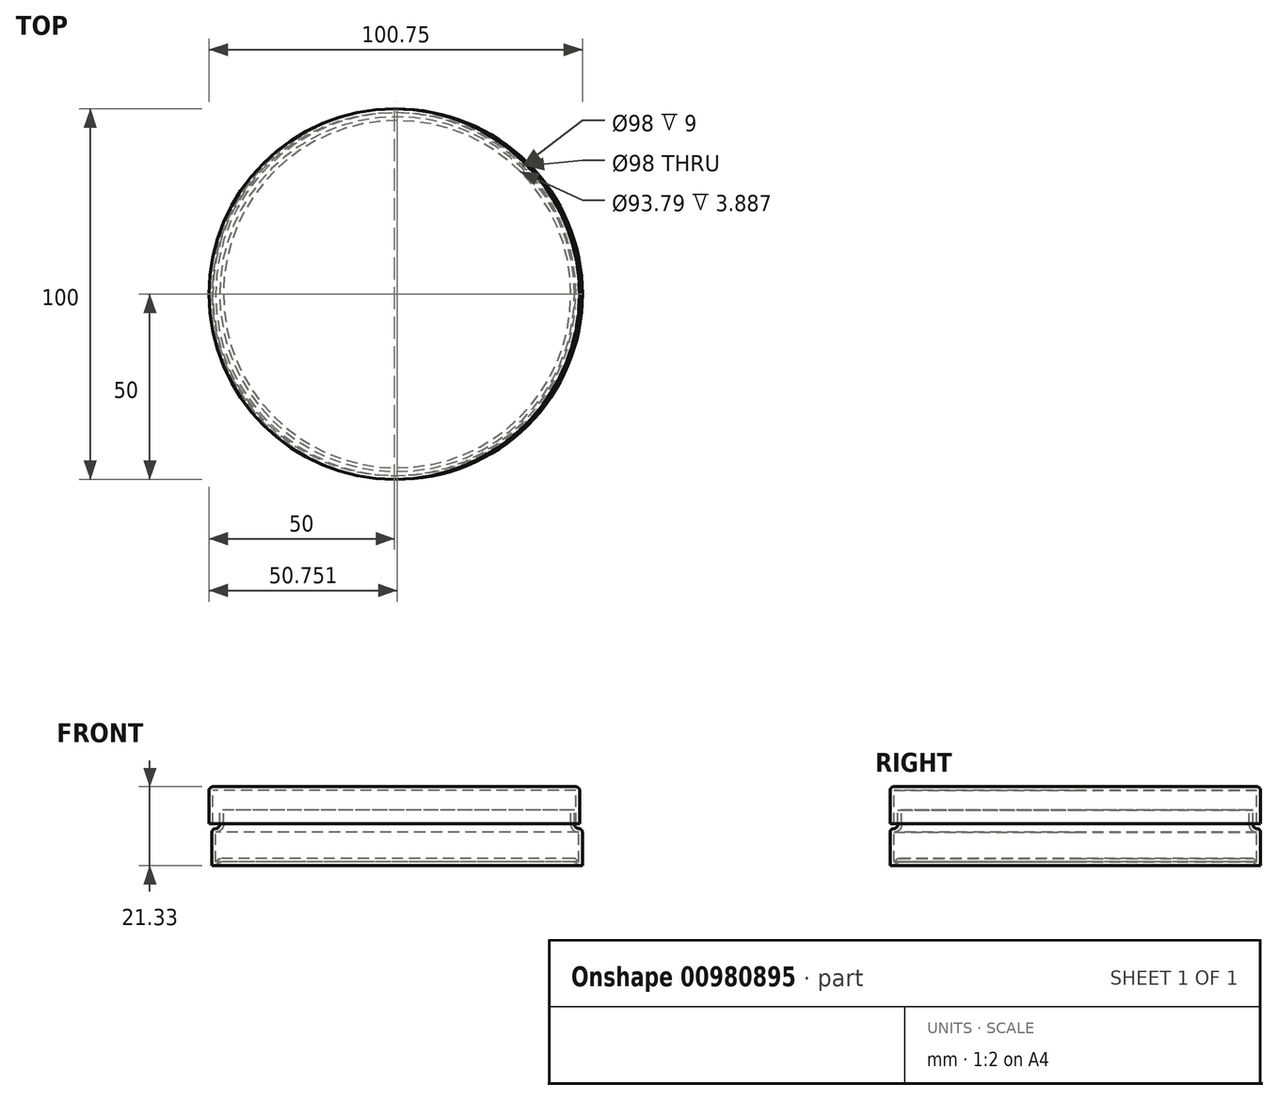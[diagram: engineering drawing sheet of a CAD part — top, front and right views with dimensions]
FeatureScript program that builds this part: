
annotation { "Feature Type Name" : "Feature", "Feature Type Description" : "" }
export const myFeature = defineFeature(function(context is Context, id is Id, definition is map)
    precondition{}
    {
        {
            var Q0;
            Q0=qCreatedBy(makeId("Front.planeOp"),FACE);
            var sketch = newSketch(context, id + "F0", { "sketchPlane" : qUnion([Q0])});
            skLineSegment(sketch, "E0", {"start": v(-50, 0) * mm, "end": v(-50, 9) * mm});
            skLineSegment(sketch, "E1", {"start": v(-49, 10) * mm, "end": v(0, 10) * mm});
            skLineSegment(sketch, "E2", {"start": v(0, 10) * mm, "end": v(0, 9) * mm});
            skLineSegment(sketch, "E3", {"start": v(0, 9) * mm, "end": v(-49, 9) * mm});
            skLineSegment(sketch, "E4", {"start": v(-49, 9) * mm, "end": v(-49, 0) * mm});
            skLineSegment(sketch, "E5", {"start": v(-49, 0) * mm, "end": v(-50, 0) * mm});
            skPoint(sketch, "E6.visualSharp", {"position": v(-50, 10) * mm});
            skArc(sketch, "E6.filletArc", {"start": v(-49, 10) * mm, "mid": v(-49.7, 9.7) * mm, "end": v(-50, 9) * mm});
            skSolve(sketch);
        }
        {
            var Q0;
            Q0=qCreatedBy(makeId("Front.planeOp"),FACE);
            var sketch = newSketch(context, id + "F1", { "sketchPlane" : qUnion([Q0])});
            skLineSegment(sketch, "E7", {"start": v(-46.15, 3.67) * mm, "end": v(-46.15, -0.22) * mm});
            skLineSegment(sketch, "E8", {"start": v(-48.25, -10.33) * mm, "end": v(-48.25, -10.33) * mm});
            skLineSegment(sketch, "E9", {"start": v(-48.25, -10.33) * mm, "end": v(-47.54, -9.62) * mm});
            skLineSegment(sketch, "E10", {"start": v(-46.83, -9.33) * mm, "end": v(0.75, -9.33) * mm});
            skLineSegment(sketch, "E11", {"start": v(0.75, -9.33) * mm, "end": v(0.75, -10.33) * mm});
            skLineSegment(sketch, "E12", {"start": v(0.75, -10.33) * mm, "end": v(-46.83, -10.33) * mm});
            skLineSegment(sketch, "E13", {"start": v(-47.54, -10.62) * mm, "end": v(-47.96, -11.04) * mm});
            skLineSegment(sketch, "E14", {"start": v(-47.15, 3.67) * mm, "end": v(-46.15, 3.67) * mm});
            skLineSegment(sketch, "E15", {"start": v(-49.25, -11.33) * mm, "end": v(-49.25, -2.3) * mm});
            skLineSegment(sketch, "E16", {"start": v(-48.48, -1.32) * mm, "end": v(-47.92, -1.2) * mm});
            skLineSegment(sketch, "E17", {"start": v(-47.15, -0.22) * mm, "end": v(-47.15, 3.67) * mm});
            skPoint(sketch, "E18.visualSharp", {"position": v(-47.25, -9.33) * mm});
            skArc(sketch, "E18.filletArc", {"start": v(-46.83, -9.33) * mm, "mid": v(-47.22, -9.4) * mm, "end": v(-47.54, -9.62) * mm});
            skPoint(sketch, "E19.visualSharp", {"position": v(-47.25, -10.33) * mm});
            skArc(sketch, "E19.filletArc", {"start": v(-46.83, -10.33) * mm, "mid": v(-47.22, -10.4) * mm, "end": v(-47.54, -10.62) * mm});
            skPoint(sketch, "E20.visualSharp", {"position": v(-48.25, -11.33) * mm});
            skArc(sketch, "E20.filletArc", {"start": v(-48.66, -11.33) * mm, "mid": v(-48.28, -11.26) * mm, "end": v(-47.96, -11.04) * mm});
            skPoint(sketch, "E21.visualSharp", {"position": v(-49.25, -11.33) * mm});
            skPoint(sketch, "E22.visualSharp", {"position": v(-49.25, -1.5) * mm});
            skArc(sketch, "E22.filletArc", {"start": v(-48.48, -1.32) * mm, "mid": v(-49.03, -1.68) * mm, "end": v(-49.25, -2.3) * mm});
            skPoint(sketch, "E23.visualSharp", {"position": v(-47.15, -1.01) * mm});
            skArc(sketch, "E23.filletArc", {"start": v(-47.92, -1.2) * mm, "mid": v(-47.36, -0.84) * mm, "end": v(-47.15, -0.22) * mm});
            skLineSegment(sketch, "E24", {"start": v(-48.25, -10.33) * mm, "end": v(-48.25, -2.3) * mm});
            skLineSegment(sketch, "E25", {"start": v(-48.25, -2.3) * mm, "end": v(-47.69, -2.17) * mm});
            skPoint(sketch, "E26.visualSharp", {"position": v(-46.15, -1.8) * mm});
            skArc(sketch, "E26.filletArc", {"start": v(-47.69, -2.17) * mm, "mid": v(-46.58, -1.46) * mm, "end": v(-46.15, -0.22) * mm});
            skLineSegment(sketch, "E27", {"start": v(-48.66, -11.33) * mm, "end": v(-49.25, -11.33) * mm});
            skSolve(sketch);
        }
        {
            var Q0;
            Q0 = qSketchRegion(id + "F0", true);
            var Q1;
            Q1=sQuery(id+"F0.wireOp",EDGE,"E2");
            revolve(context, id + "F2", {"surfaceOperationType" : NewSurfaceOperationType.NEW, "entities" : qUnion([Q0]), "axis" : qUnion([Q1]), "revolveType" : RevolveType.FULL});
        }
        {
            var Q0;
            Q0 = qSketchRegion(id + "F1", true);
            var Q1;
            Q1=sQuery(id+"F1.wireOp",EDGE,"E11");
            revolve(context, id + "F3", {"surfaceOperationType" : NewSurfaceOperationType.NEW, "entities" : qUnion([Q0]), "axis" : qUnion([Q1]), "revolveType" : RevolveType.FULL});
        }
    });
